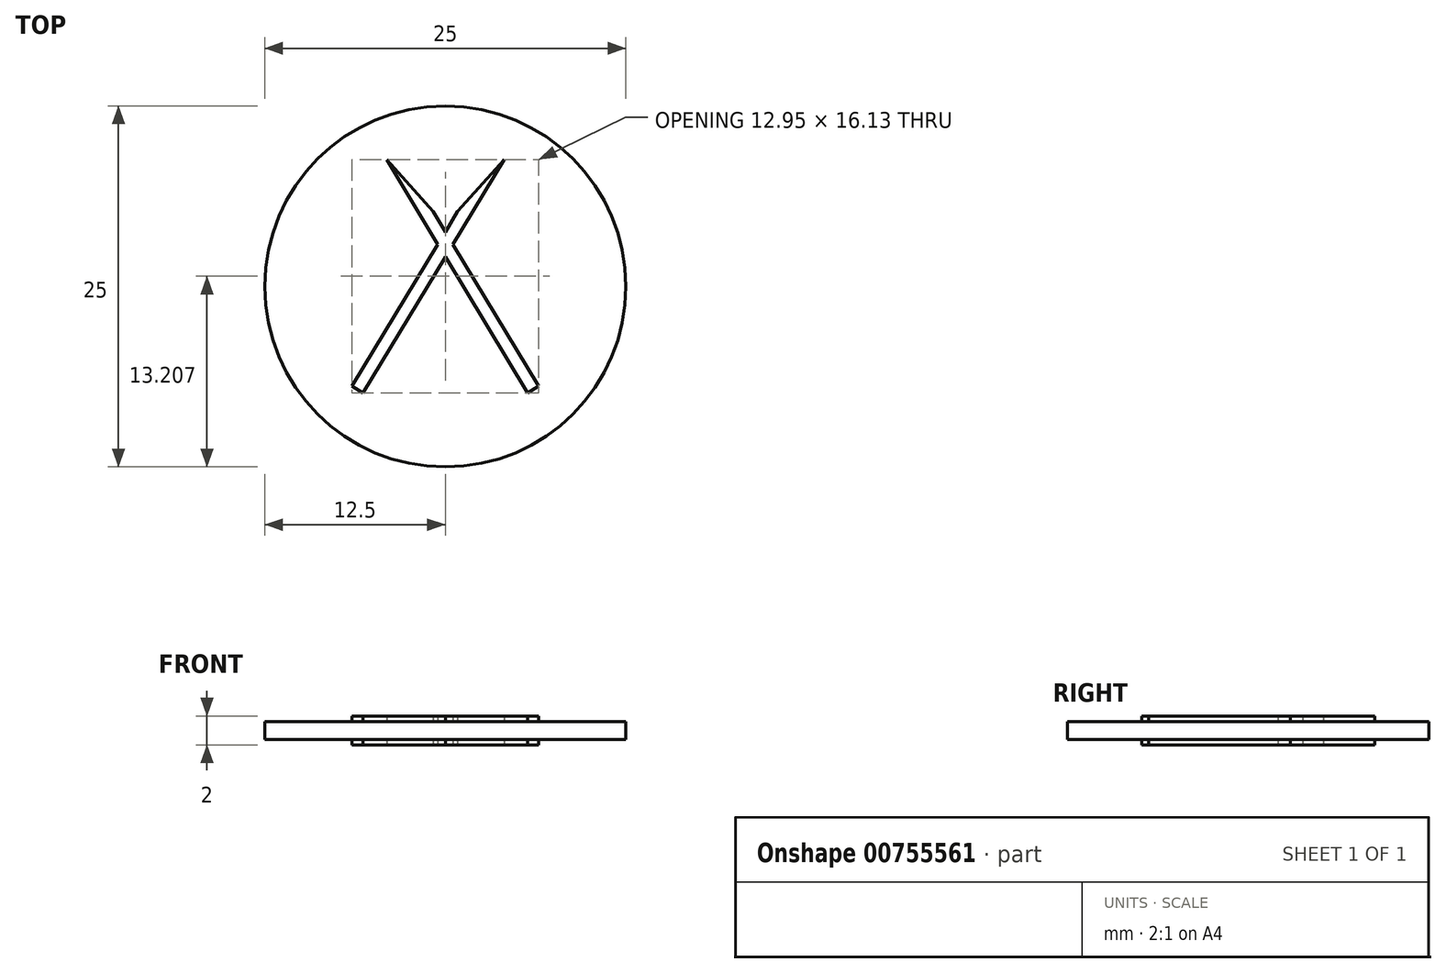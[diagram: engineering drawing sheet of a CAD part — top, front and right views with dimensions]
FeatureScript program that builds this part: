
annotation { "Feature Type Name" : "Feature", "Feature Type Description" : "" }
export const myFeature = defineFeature(function(context is Context, id is Id, definition is map)
    precondition{}
    {
        {
            var Q0;
            Q0=qCreatedBy(makeId("Top.planeOp"),FACE);
            var sketch = newSketch(context, id + "F0", { "sketchPlane" : qUnion([Q0])});
            skCircle(sketch, "E0", {"center": v(0, 0) * mm, "radius": 12.5 * mm});
            skLineSegment(sketch, "E1", {"start": v(-0.85, 5.2) * mm, "end": v(6.47, -6.9) * mm});
            skLineSegment(sketch, "E2", {"start": v(6.47, -6.9) * mm, "end": v(5.71, -7.36) * mm});
            skLineSegment(sketch, "E3", {"start": v(5.71, -7.36) * mm, "end": v(-4.06, 8.77) * mm});
            skLineSegment(sketch, "E4", {"start": v(-0.85, 5.2) * mm, "end": v(-4.06, 8.77) * mm});
            skLineSegment(sketch, "E5", {"start": v(-0.87, 5.2) * mm, "end": v(-0.89, 5.25) * mm});
            skLineSegment(sketch, "E6", {"start": v(-1.9, 5.2) * mm, "end": v(-0.87, 5.2) * mm});
            skLineSegment(sketch, "E7", {"start": v(-1.9, 5.2) * mm, "end": v(-1.9, 5.2) * mm});
            skLineSegment(sketch, "E8", {"start": v(-1.9, 5.2) * mm, "end": v(-0.85, 3.47) * mm});
            skLineSegment(sketch, "E9.MirrorCS", {"start": v(1.9, 5.2) * mm, "end": v(0.87, 5.2) * mm});
            skLineSegment(sketch, "E10.MirrorCS", {"start": v(1.9, 5.2) * mm, "end": v(1.9, 5.2) * mm});
            skLineSegment(sketch, "E11.MirrorCS", {"start": v(1.9, 5.2) * mm, "end": v(0.85, 3.47) * mm});
            skLineSegment(sketch, "E12.MirrorCS", {"start": v(0.85, 5.2) * mm, "end": v(4.06, 8.77) * mm});
            skLineSegment(sketch, "E13.MirrorCS", {"start": v(-5.71, -7.36) * mm, "end": v(4.06, 8.77) * mm});
            skLineSegment(sketch, "E14.MirrorCS", {"start": v(0.85, 5.2) * mm, "end": v(-6.47, -6.9) * mm});
            skLineSegment(sketch, "E15.MirrorCS", {"start": v(0.87, 5.2) * mm, "end": v(0.89, 5.25) * mm});
            skLineSegment(sketch, "E16.MirrorCS", {"start": v(-6.47, -6.9) * mm, "end": v(-5.71, -7.36) * mm});
            skSolve(sketch);
        }
        {
            var Q0;
            Q0=makeQuery(id+"F0.imprint","IMPRINT",FACE,{"disambiguationData":[TD([[makeQuery(id+"F0.imprint","IMPRINT",EDGE,{"derivedFrom":sQuery(id+"F0.wireOp",EDGE,"E0")}),1.0]])]});
            extrude(context, id + "F1", {"entities" : qUnion([Q0]), "endBound" : BoundingType.SYMMETRIC, "depth" : 1.25 * mm, "offsetDistance" : 25 * mm});
        }
        {
            var Q0;
            {var subQ9=sQuery(id+"F0.wireOp",EDGE,"E6");Q0=makeQuery(id+"F0.imprint","IMPRINT",FACE,{"disambiguationData":[TD([[makeQuery(id+"F0.imprint","IMPRINT",EDGE,{"derivedFrom":subQ9}),-1.0]])]});}
            var Q1;
            {var subQ9=sQuery(id+"F0.wireOp",EDGE,"E9.MirrorCS");Q1=makeQuery(id+"F0.imprint","IMPRINT",FACE,{"disambiguationData":[TD([[makeQuery(id+"F0.imprint","IMPRINT",EDGE,{"derivedFrom":subQ9}),1.0]])]});}
            var Q2;
            {var subQ0=sQuery(id+"F0.wireOp",EDGE,"E9.MirrorCS");Q2=makeQuery(id+"F0.imprint","IMPRINT",FACE,{"disambiguationData":[TD([[makeQuery(id+"F0.imprint","IMPRINT",EDGE,{"derivedFrom":subQ0}),-1.0]])]});}
            var Q3;
            {var subQ3=sQuery(id+"F0.wireOp",EDGE,"E6");Q3=makeQuery(id+"F0.imprint","IMPRINT",FACE,{"disambiguationData":[TD([[makeQuery(id+"F0.imprint","IMPRINT",EDGE,{"derivedFrom":subQ3}),1.0]])]});}
            var Q4;
            {var subQ0=sQuery(id+"F0.wireOp",EDGE,"E14.MirrorCS");var subQ1=sQuery(id+"F0.wireOp",EDGE,"E1");var subQ2=makeQuery(id+"F0.imprint","INTERSECT",VERTEX,{"derivedFrom":[subQ1,subQ0]});Q4=makeQuery(id+"F0.imprint","IMPRINT",FACE,{"disambiguationData":[TD([[makeQuery(id+"F0.imprint","IMPRINT",EDGE,{"disambiguationData":[TD([[subQ2,-1.0]])],"derivedFrom":subQ1}),-1.0]])]});}
            var Q5;
            {var subQ5=sQuery(id+"F0.wireOp",EDGE,"E16.MirrorCS");Q5=makeQuery(id+"F0.imprint","IMPRINT",FACE,{"disambiguationData":[TD([[makeQuery(id+"F0.imprint","IMPRINT",EDGE,{"derivedFrom":subQ5}),1.0]])]});}
            var Q6;
            {var subQ0=sQuery(id+"F0.wireOp",EDGE,"E2");Q6=makeQuery(id+"F0.imprint","IMPRINT",FACE,{"disambiguationData":[TD([[makeQuery(id+"F0.imprint","IMPRINT",EDGE,{"derivedFrom":subQ0}),-1.0]])]});}
            extrude(context, id + "F2", {"entities" : qUnion([Q0, Q1, Q2, Q3, Q4, Q5, Q6]), "operationType" : NewBodyOperationType.ADD, "endBound" : BoundingType.SYMMETRIC, "depth" : 2 * mm, "offsetDistance" : 25 * mm});
        }
    });
